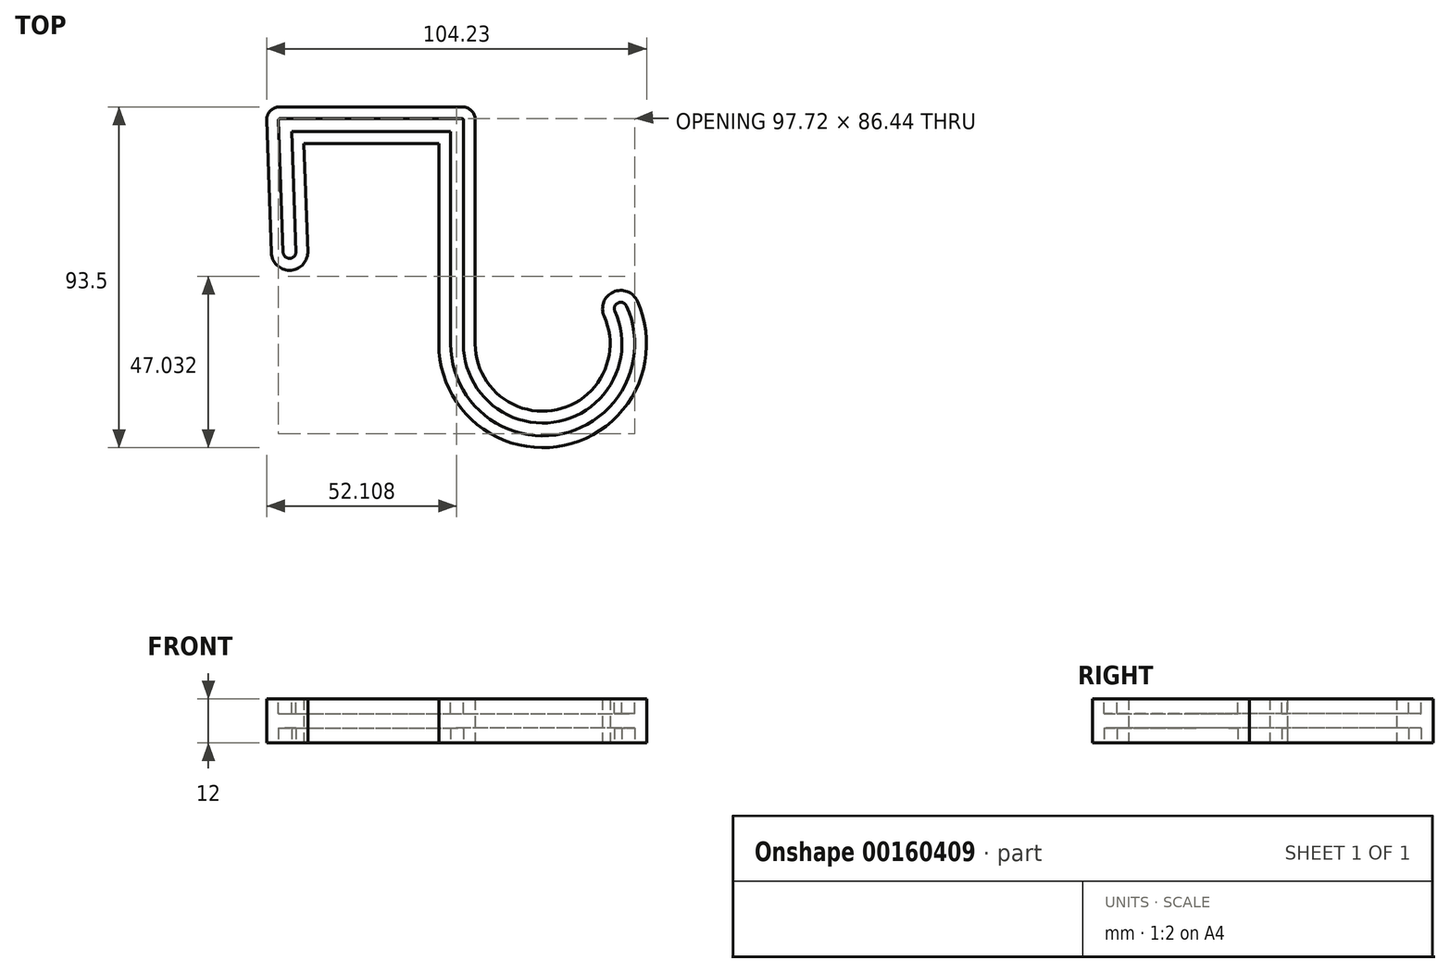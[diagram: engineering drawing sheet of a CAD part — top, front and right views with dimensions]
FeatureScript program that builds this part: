
annotation { "Feature Type Name" : "Feature", "Feature Type Description" : "" }
export const myFeature = defineFeature(function(context is Context, id is Id, definition is map)
    precondition{}
    {
        {
            var Q0;
            Q0=qCreatedBy(makeId("Top.planeOp"),FACE);
            var sketch = newSketch(context, id + "F0", { "sketchPlane" : qUnion([Q0])});
            skLineSegment(sketch, "E0", {"start": v(-46.37, 38.41) * mm, "end": v(10.99, 38.41) * mm});
            skLineSegment(sketch, "E1", {"start": v(10.99, 38.41) * mm, "end": v(10.99, -26.59) * mm});
            skLineSegment(sketch, "E2.1", {"start": v(0.99, 28.41) * mm, "end": v(0.99, -26.59) * mm});
            skLineSegment(sketch, "E2.2", {"start": v(-36.01, 28.41) * mm, "end": v(0.99, 28.41) * mm});
            skArc(sketch, "E3", {"start": v(10.99, -26.59) * mm, "mid": v(29.49, -45.09) * mm, "end": v(47.99, -26.59) * mm, "construction": true});
            skArc(sketch, "E4", {"start": v(0.99, -26.59) * mm, "mid": v(35.47, -54.45) * mm, "end": v(55.47, -14.88) * mm});
            skArc(sketch, "E5", {"start": v(10.99, -26.59) * mm, "mid": v(33.37, -44.68) * mm, "end": v(46.35, -19) * mm});
            skArc(sketch, "E6", {"start": v(55.47, -14.88) * mm, "mid": v(48.86, -12.38) * mm, "end": v(46.35, -19) * mm});
            skLineSegment(sketch, "E7", {"start": v(-36.01, 28.41) * mm, "end": v(-34.97, -1.57) * mm});
            skLineSegment(sketch, "E8", {"start": v(-46.37, 38.41) * mm, "end": v(-44.97, -1.57) * mm});
            skLineSegment(sketch, "E9", {"start": v(-17.7, 38.41) * mm, "end": v(-17.7, 28.41) * mm, "construction": true});
            skLineSegment(sketch, "E10", {"start": v(10.99, 5.91) * mm, "end": v(0.99, 5.91) * mm, "construction": true});
            skLineSegment(sketch, "E11", {"start": v(29.49, -45.09) * mm, "end": v(29.49, -55.09) * mm, "construction": true});
            skLineSegment(sketch, "E12", {"start": v(-45.67, 18.42) * mm, "end": v(-35.68, 18.77) * mm, "construction": true});
            skLineSegment(sketch, "E13", {"start": v(-34.97, -1.57) * mm, "end": v(-44.97, -1.57) * mm, "construction": true});
            skArc(sketch, "E14", {"start": v(-44.97, -1.57) * mm, "mid": v(-39.97, -6.4) * mm, "end": v(-34.97, -1.57) * mm});
            skSolve(sketch);
        }
        {
            var Q0;
            Q0 = qSketchRegion(id + "F0", true);
            extrude(context, id + "F1", {"entities" : qUnion([Q0]), "depth" : 12 * mm});
        }
        {
            var Q0;
            Q0=makeQuery(id+"F1.opExtrude","SWEPT_EDGE",EDGE,{"disambiguationData":[OSD([sQuery(id+"F0.wireOp",EDGE,"E0"),sQuery(id+"F0.wireOp",EDGE,"E1")])]});
            var Q1;
            Q1=makeQuery(id+"F1.opExtrude","SWEPT_EDGE",EDGE,{"disambiguationData":[OSD([sQuery(id+"F0.wireOp",EDGE,"4GFNpA2f-gsCF-CoUM-R4hG-wyUXzbRysPrt"),sQuery(id+"F0.wireOp",EDGE,"E0")])]});
            fillet(context, id + "F2", {"entities" : qUnion([Q0, Q1]), "radius" : 3.5 * mm, "tangentPropagation" : true, "allowEdgeOverflow" : false});
        }
        {
            var Q0;
            Q0=makeQuery(id+"F1.opExtrude","CAP_FACE",FACE,{"disambiguationData":[OSD([sQuery(id+"F0.wireOp",EDGE,"E0"),sQuery(id+"F0.wireOp",EDGE,"E1"),sQuery(id+"F0.wireOp",EDGE,"E2.1"),sQuery(id+"F0.wireOp",EDGE,"E2.2"),sQuery(id+"F0.wireOp",EDGE,"E4"),sQuery(id+"F0.wireOp",EDGE,"E5"),sQuery(id+"F0.wireOp",EDGE,"E6"),sQuery(id+"F0.wireOp",EDGE,"E7"),sQuery(id+"F0.wireOp",EDGE,"E8"),sQuery(id+"F0.wireOp",EDGE,"E14")])],"isStart":false});
            var sketch = newSketch(context, id + "F3", { "sketchPlane" : qUnion([Q0])});
            skLineSegment(sketch, "E15.0", {"start": v(-46.24, 34.79) * mm, "end": v(-44.97, -1.57) * mm, "construction": true});
            skLineSegment(sketch, "E15.1", {"start": v(-36.01, 28.41) * mm, "end": v(-34.97, -1.57) * mm, "construction": true});
            skArc(sketch, "E15.2", {"start": v(-44.97, -1.57) * mm, "mid": v(-39.97, -6.4) * mm, "end": v(-34.97, -1.57) * mm, "construction": true});
            skArc(sketch, "E15.3", {"start": v(-42.74, 38.41) * mm, "mid": v(-45.26, 37.34) * mm, "end": v(-46.24, 34.79) * mm, "construction": true});
            skLineSegment(sketch, "E15.4", {"start": v(-42.74, 38.41) * mm, "end": v(7.49, 38.41) * mm, "construction": true});
            skLineSegment(sketch, "E15.5", {"start": v(-36.01, 28.41) * mm, "end": v(0.99, 28.41) * mm, "construction": true});
            skLineSegment(sketch, "E15.6", {"start": v(0.99, 28.41) * mm, "end": v(0.99, -26.59) * mm, "construction": true});
            skLineSegment(sketch, "E15.7", {"start": v(10.99, 34.91) * mm, "end": v(10.99, -26.59) * mm, "construction": true});
            skArc(sketch, "E15.8", {"start": v(10.99, 34.91) * mm, "mid": v(9.96, 37.39) * mm, "end": v(7.49, 38.41) * mm, "construction": true});
            skArc(sketch, "E15.9", {"start": v(10.99, -26.59) * mm, "mid": v(33.37, -44.68) * mm, "end": v(46.35, -19) * mm, "construction": true});
            skArc(sketch, "E15.10", {"start": v(0.99, -26.59) * mm, "mid": v(35.47, -54.45) * mm, "end": v(55.47, -14.88) * mm, "construction": true});
            skArc(sketch, "E15.11", {"start": v(55.47, -14.88) * mm, "mid": v(48.86, -12.38) * mm, "end": v(46.35, -19) * mm, "construction": true});
            skArc(sketch, "E16.0", {"start": v(-42.74, 35.16) * mm, "mid": v(-42.92, 35.08) * mm, "end": v(-43, 34.9) * mm});
            skLineSegment(sketch, "E16.1", {"start": v(4.24, 31.66) * mm, "end": v(4.24, -26.59) * mm});
            skLineSegment(sketch, "E16.2", {"start": v(-39.38, 31.66) * mm, "end": v(4.24, 31.66) * mm});
            skLineSegment(sketch, "E16.3", {"start": v(-39.38, 31.66) * mm, "end": v(-38.22, -1.54) * mm});
            skArc(sketch, "E16.4", {"start": v(-41.72, -1.46) * mm, "mid": v(-40.01, -3.15) * mm, "end": v(-38.22, -1.54) * mm});
            skArc(sketch, "E16.5", {"start": v(4.24, -26.59) * mm, "mid": v(34.8, -51.28) * mm, "end": v(52.5, -16.22) * mm});
            skLineSegment(sketch, "E16.6", {"start": v(-43, 34.9) * mm, "end": v(-41.72, -1.46) * mm});
            skArc(sketch, "E16.7", {"start": v(52.5, -16.22) * mm, "mid": v(50.2, -15.34) * mm, "end": v(49.32, -17.66) * mm});
            skArc(sketch, "E16.8", {"start": v(7.74, -26.59) * mm, "mid": v(34.06, -47.85) * mm, "end": v(49.32, -17.66) * mm});
            skLineSegment(sketch, "E16.9", {"start": v(7.74, 34.91) * mm, "end": v(7.74, -26.59) * mm});
            skArc(sketch, "E16.10", {"start": v(7.74, 34.91) * mm, "mid": v(7.66, 35.09) * mm, "end": v(7.49, 35.16) * mm});
            skLineSegment(sketch, "E16.11", {"start": v(-42.74, 35.16) * mm, "end": v(7.49, 35.16) * mm});
            skSolve(sketch);
        }
        {
            var Q0;
            Q0 = qSketchRegion(id + "F3", true);
            extrude(context, id + "F4", {"entities" : qUnion([Q0]), "operationType" : NewBodyOperationType.REMOVE, "oppositeDirection" : true, "depth" : 4 * mm});
        }
        {
            var Q0;
            Q0=makeQuery(id+"F1.opExtrude","CAP_FACE",FACE,{"disambiguationData":[OSD([sQuery(id+"F0.wireOp",EDGE,"E0"),sQuery(id+"F0.wireOp",EDGE,"E1"),sQuery(id+"F0.wireOp",EDGE,"E2.1"),sQuery(id+"F0.wireOp",EDGE,"E2.2"),sQuery(id+"F0.wireOp",EDGE,"E4"),sQuery(id+"F0.wireOp",EDGE,"E5"),sQuery(id+"F0.wireOp",EDGE,"E6"),sQuery(id+"F0.wireOp",EDGE,"E7"),sQuery(id+"F0.wireOp",EDGE,"E8"),sQuery(id+"F0.wireOp",EDGE,"E14")])],"isStart":true});
            var sketch = newSketch(context, id + "F5", { "sketchPlane" : qUnion([Q0])});
            skLineSegment(sketch, "E17.0", {"start": v(-36.01, -28.41) * mm, "end": v(-34.97, 1.57) * mm, "construction": true});
            skArc(sketch, "E17.1", {"start": v(-44.97, 1.57) * mm, "mid": v(-39.97, 6.4) * mm, "end": v(-34.97, 1.57) * mm, "construction": true});
            skLineSegment(sketch, "E17.2", {"start": v(-46.24, -34.79) * mm, "end": v(-44.97, 1.57) * mm, "construction": true});
            skArc(sketch, "E17.3", {"start": v(-46.24, -34.79) * mm, "mid": v(-45.26, -37.34) * mm, "end": v(-42.74, -38.41) * mm, "construction": true});
            skLineSegment(sketch, "E17.4", {"start": v(-42.74, -38.41) * mm, "end": v(7.49, -38.41) * mm, "construction": true});
            skLineSegment(sketch, "E17.5", {"start": v(-36.01, -28.41) * mm, "end": v(0.99, -28.41) * mm, "construction": true});
            skArc(sketch, "E17.6", {"start": v(7.49, -38.41) * mm, "mid": v(9.96, -37.39) * mm, "end": v(10.99, -34.91) * mm, "construction": true});
            skLineSegment(sketch, "E17.7", {"start": v(10.99, -34.91) * mm, "end": v(10.99, 26.59) * mm, "construction": true});
            skLineSegment(sketch, "E17.8", {"start": v(0.99, -28.41) * mm, "end": v(0.99, 26.59) * mm, "construction": true});
            skArc(sketch, "E17.9", {"start": v(0.99, 26.59) * mm, "mid": v(35.47, 54.45) * mm, "end": v(55.47, 14.88) * mm, "construction": true});
            skArc(sketch, "E17.10", {"start": v(10.99, 26.59) * mm, "mid": v(33.37, 44.68) * mm, "end": v(46.35, 19) * mm, "construction": true});
            skArc(sketch, "E17.11", {"start": v(55.47, 14.88) * mm, "mid": v(48.86, 12.38) * mm, "end": v(46.35, 19) * mm, "construction": true});
            skLineSegment(sketch, "E18.0", {"start": v(-43, -34.9) * mm, "end": v(-41.72, 1.46) * mm});
            skArc(sketch, "E18.1", {"start": v(4.24, 26.59) * mm, "mid": v(34.8, 51.28) * mm, "end": v(52.5, 16.22) * mm});
            skLineSegment(sketch, "E18.2", {"start": v(4.24, -31.66) * mm, "end": v(4.24, 26.59) * mm});
            skLineSegment(sketch, "E18.3", {"start": v(-39.38, -31.66) * mm, "end": v(4.24, -31.66) * mm});
            skLineSegment(sketch, "E18.4", {"start": v(-39.38, -31.66) * mm, "end": v(-38.22, 1.54) * mm});
            skArc(sketch, "E18.5", {"start": v(52.5, 16.22) * mm, "mid": v(50.2, 15.34) * mm, "end": v(49.32, 17.66) * mm});
            skArc(sketch, "E18.6", {"start": v(-41.72, 1.46) * mm, "mid": v(-40.01, 3.15) * mm, "end": v(-38.22, 1.54) * mm});
            skArc(sketch, "E18.7", {"start": v(7.74, 26.59) * mm, "mid": v(34.06, 47.85) * mm, "end": v(49.32, 17.66) * mm});
            skLineSegment(sketch, "E18.8", {"start": v(7.74, -34.91) * mm, "end": v(7.74, 26.59) * mm});
            skArc(sketch, "E18.9", {"start": v(7.49, -35.16) * mm, "mid": v(7.66, -35.09) * mm, "end": v(7.74, -34.91) * mm});
            skLineSegment(sketch, "E18.10", {"start": v(-42.74, -35.16) * mm, "end": v(7.49, -35.16) * mm});
            skArc(sketch, "E18.11", {"start": v(-43, -34.9) * mm, "mid": v(-42.92, -35.08) * mm, "end": v(-42.74, -35.16) * mm});
            skSolve(sketch);
        }
        {
            var Q0;
            Q0 = qSketchRegion(id + "F5", true);
            extrude(context, id + "F6", {"entities" : qUnion([Q0]), "operationType" : NewBodyOperationType.REMOVE, "oppositeDirection" : true, "depth" : 4 * mm});
        }
    });
